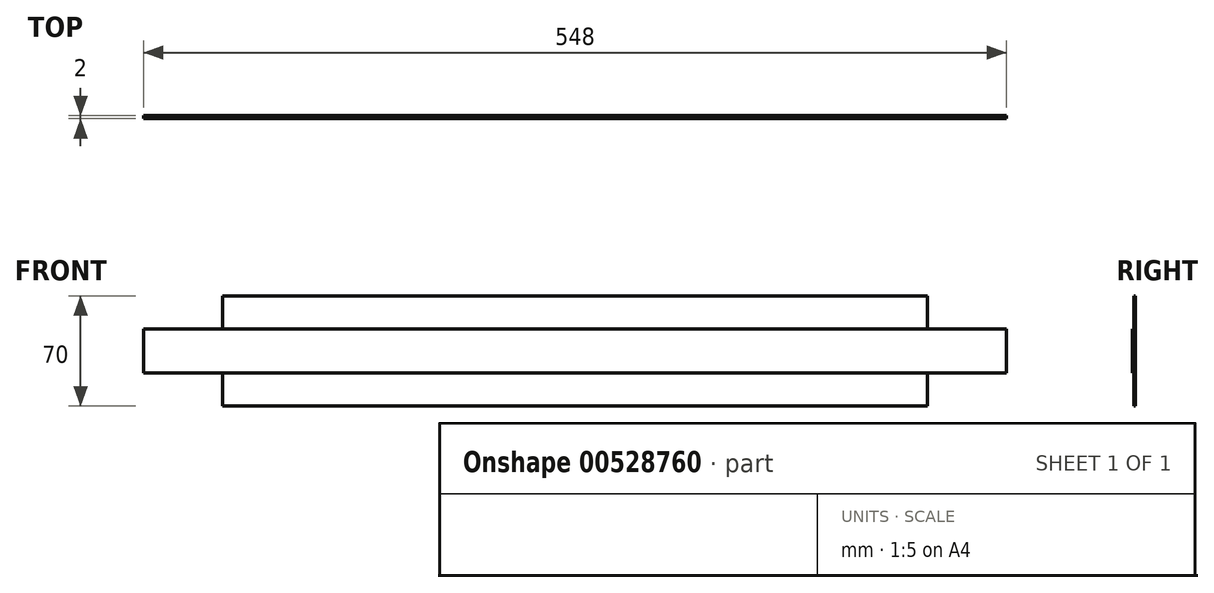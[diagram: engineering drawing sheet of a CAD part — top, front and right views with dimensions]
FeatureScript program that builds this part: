
annotation { "Feature Type Name" : "Feature", "Feature Type Description" : "" }
export const myFeature = defineFeature(function(context is Context, id is Id, definition is map)
    precondition{}
    {
        {
            var Q0;
            Q0=qCreatedBy(makeId("Front.planeOp"),FACE);
            var sketch = newSketch(context, id + "F0", { "sketchPlane" : qUnion([Q0])});
            skLineSegment(sketch, "E0.bottom", {"start": v(-19.31, 0) * mm, "end": v(428.69, 0) * mm});
            skLineSegment(sketch, "E0.top", {"start": v(-19.31, 98) * mm, "end": v(428.69, 98) * mm});
            skLineSegment(sketch, "E0.left", {"start": v(-69.31, 35) * mm, "end": v(-69.31, 63) * mm});
            skLineSegment(sketch, "E0.right", {"start": v(478.69, 35) * mm, "end": v(478.69, 63) * mm});
            skLineSegment(sketch, "E1.top", {"start": v(-69.31, 63) * mm, "end": v(-19.31, 63) * mm});
            skLineSegment(sketch, "E1.right", {"start": v(-19.31, 98) * mm, "end": v(-19.31, 63) * mm});
            skLineSegment(sketch, "E2.top", {"start": v(-69.31, 35) * mm, "end": v(-19.31, 35) * mm});
            skLineSegment(sketch, "E2.right", {"start": v(-19.31, 0) * mm, "end": v(-19.31, 35) * mm});
            skPoint(sketch, "E3.orphan", {"position": v(-69.31, 0) * mm});
            skLineSegment(sketch, "E4.top", {"start": v(478.69, 63) * mm, "end": v(428.69, 63) * mm});
            skLineSegment(sketch, "E4.right", {"start": v(428.69, 98) * mm, "end": v(428.69, 63) * mm});
            skLineSegment(sketch, "E5.top", {"start": v(478.69, 35) * mm, "end": v(428.69, 35) * mm});
            skLineSegment(sketch, "E5.right", {"start": v(428.69, 0) * mm, "end": v(428.69, 35) * mm});
            skLineSegment(sketch, "E6.top", {"start": v(-19.31, 84) * mm, "end": v(428.69, 84) * mm});
            skLineSegment(sketch, "E6.left", {"start": v(-19.31, 98) * mm, "end": v(-19.31, 84) * mm});
            skLineSegment(sketch, "E6.right", {"start": v(428.69, 98) * mm, "end": v(428.69, 84) * mm});
            skLineSegment(sketch, "E7.top", {"start": v(-19.31, 63) * mm, "end": v(428.69, 63) * mm});
            skLineSegment(sketch, "E7.left", {"start": v(-19.31, 84) * mm, "end": v(-19.31, 63) * mm});
            skLineSegment(sketch, "E7.right", {"start": v(428.69, 84) * mm, "end": v(428.69, 63) * mm});
            skLineSegment(sketch, "E8.top", {"start": v(-19.31, 14) * mm, "end": v(428.69, 14) * mm});
            skLineSegment(sketch, "E8.left", {"start": v(-19.31, 0) * mm, "end": v(-19.31, 14) * mm});
            skLineSegment(sketch, "E8.right", {"start": v(428.69, 0) * mm, "end": v(428.69, 14) * mm});
            skLineSegment(sketch, "E9.bottom", {"start": v(-19.31, 35) * mm, "end": v(428.69, 35) * mm});
            skLineSegment(sketch, "E9.left", {"start": v(-19.31, 35) * mm, "end": v(-19.31, 14) * mm});
            skLineSegment(sketch, "E9.right", {"start": v(428.69, 35) * mm, "end": v(428.69, 14) * mm});
            skLineSegment(sketch, "E10", {"start": v(428.69, 84) * mm, "end": v(-19.31, 84) * mm});
            skSolve(sketch);
        }
        {
            var Q0;
            Q0=makeQuery(id+"F0.imprint","IMPRINT",FACE,{"disambiguationData":[TD([[makeQuery(id+"F0.imprint","IMPRINT",EDGE,{"derivedFrom":sQuery(id+"F0.wireOp",EDGE,"E0.top")}),-1.0]])]});
            var Q1;
            Q1=makeQuery(id+"F0.imprint","IMPRINT",FACE,{"disambiguationData":[TD([[makeQuery(id+"F0.imprint","IMPRINT",EDGE,{"derivedFrom":sQuery(id+"F0.wireOp",EDGE,"E0.left")}),-1.0]])]});
            var Q2;
            Q2=makeQuery(id+"F0.imprint","IMPRINT",FACE,{"disambiguationData":[TD([[makeQuery(id+"F0.imprint","IMPRINT",EDGE,{"derivedFrom":sQuery(id+"F0.wireOp",EDGE,"E0.bottom")}),1.0]])]});
            extrude(context, id + "F1", {"entities" : qUnion([Q0, Q1, Q2]), "depth" : 2 * mm, "offsetDistance" : 25 * mm});
        }
        {
            var Q0;
            Q0=makeQuery(id+"F0.imprint","IMPRINT",FACE,{"disambiguationData":[TD([[makeQuery(id+"F0.imprint","IMPRINT",EDGE,{"derivedFrom":sQuery(id+"F0.wireOp",EDGE,"E7.top")}),1.0]])]});
            var Q1;
            Q1=makeQuery(id+"F0.imprint","IMPRINT",FACE,{"disambiguationData":[TD([[makeQuery(id+"F0.imprint","IMPRINT",EDGE,{"derivedFrom":sQuery(id+"F0.wireOp",EDGE,"E9.bottom")}),-1.0]])]});
            extrude(context, id + "F2", {"entities" : qUnion([Q0, Q1]), "depth" : 1 * mm, "offsetDistance" : 25 * mm});
        }
    });
